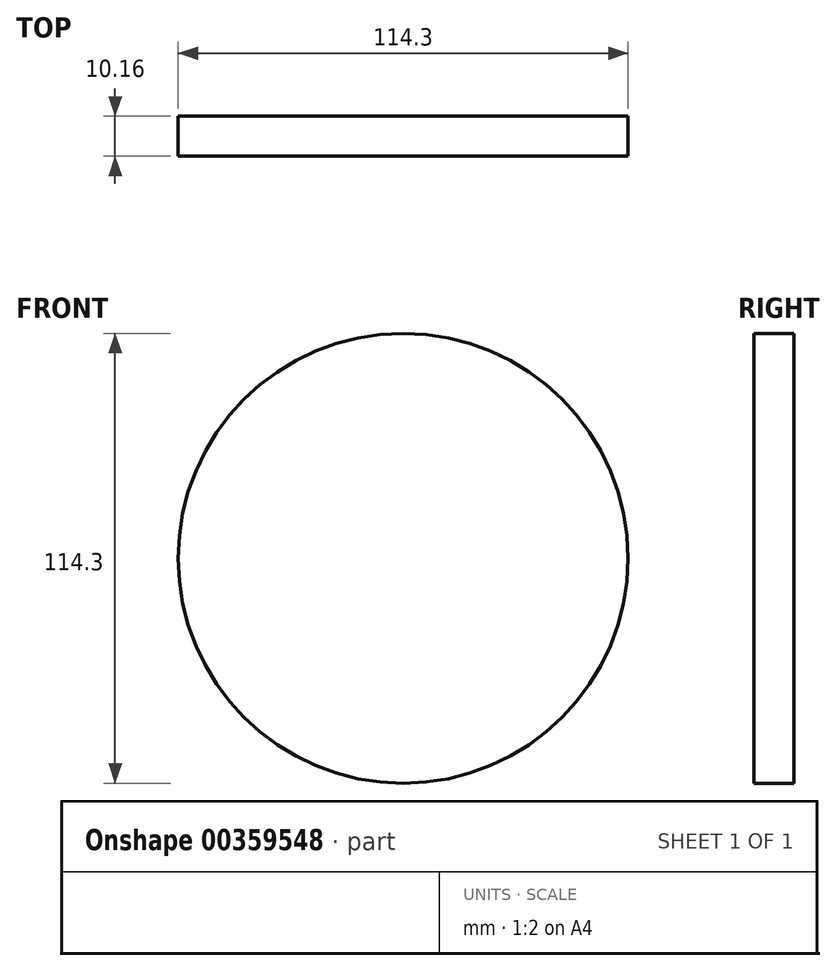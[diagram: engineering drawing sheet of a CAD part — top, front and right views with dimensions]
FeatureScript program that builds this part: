
annotation { "Feature Type Name" : "Feature", "Feature Type Description" : "" }
export const myFeature = defineFeature(function(context is Context, id is Id, definition is map)
    precondition{}
    {
        {
            var Q0;
            Q0=qCreatedBy(makeId("Front.planeOp"),FACE);
            var sketch = newSketch(context, id + "F0", { "sketchPlane" : qUnion([Q0])});
            skCircle(sketch, "E0", {"center": v(0, 0) * mm, "radius": 57.15 * mm});
            skPoint(sketch, "E1", {"position": v(0, 57.15) * mm});
            skPoint(sketch, "E2", {"position": v(0, -57.15) * mm});
            skSolve(sketch);
        }
        {
            var Q0;
            Q0=makeQuery(id+"F0.imprint","IMPRINT",FACE,{"disambiguationData":[TD([[makeQuery(id+"F0.imprint","IMPRINT",EDGE,{"derivedFrom":sQuery(id+"F0.wireOp",EDGE,"E0")}),1.0]])]});
            extrude(context, id + "F1", {"entities" : qUnion([Q0]), "depth" : 10.16 * mm});
        }
    });
